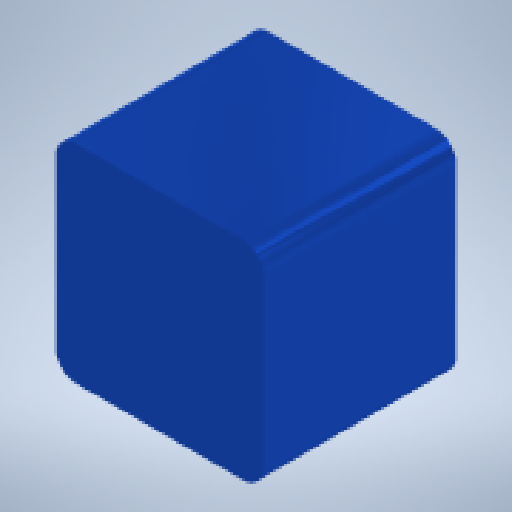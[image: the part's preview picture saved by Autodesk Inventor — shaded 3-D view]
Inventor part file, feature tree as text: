
AUTODESK INVENTOR PART (.ipt)
format: ipt  version: 2023 (Build 270158000, 158)  size: 136,192 bytes
history: native  units: mm
features: extrude x2, sketch x2, fillet x1
ambient origin geometry x8: Origin, YZ Plane, XZ Plane, XY Plane, X Axis, Y Axis, Z Axis, Center Point
bodies: Solid1 (feature_tree)
feature tree (5):
  extrude  "Extrusion1"  Depth=50.0mm
  fillet  "Fillet1"  Radius=46.5mm
  extrude  "Extrusion2"  Depth=5.0mm
  sketch  "Sketch1"  dims[d0=50.0mm d1=50.0mm d2=46.5mm d3=0.0mm]
  sketch  "Sketch2"  dims[d4=5.0mm d5=36.0mm d6=5.0mm d7=0.0mm]
